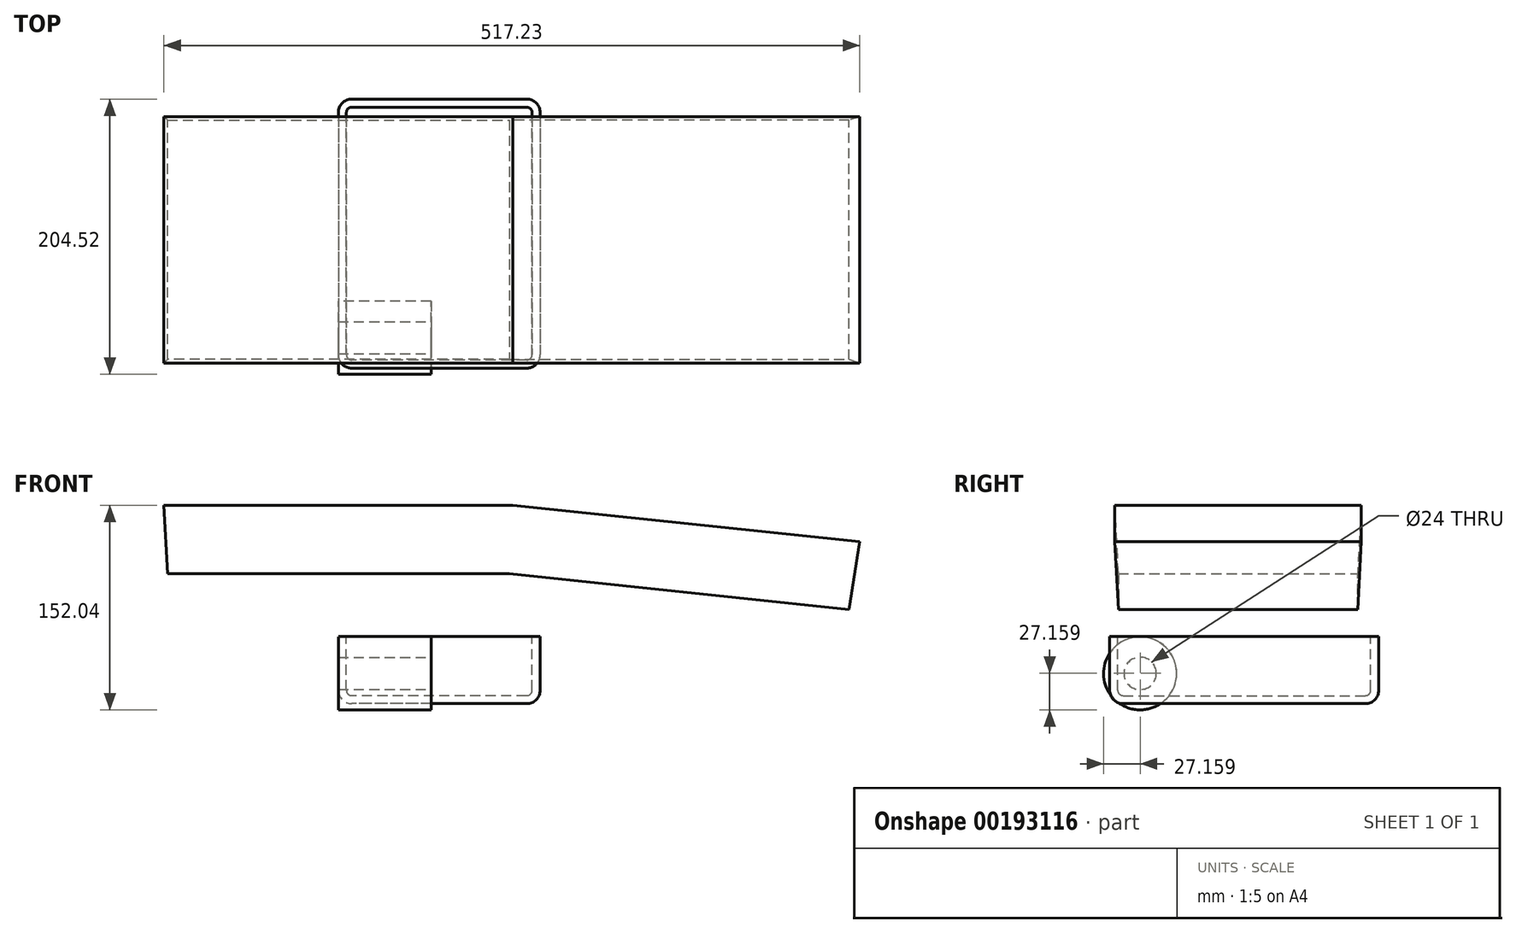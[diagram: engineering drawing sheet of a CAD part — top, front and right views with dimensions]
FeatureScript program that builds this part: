
annotation { "Feature Type Name" : "Feature", "Feature Type Description" : "" }
export const myFeature = defineFeature(function(context is Context, id is Id, definition is map)
    precondition{}
    {
        {
            var Q0;
            Q0=qCreatedBy(makeId("Top.planeOp"),FACE);
            var sketch = newSketch(context, id + "F0", { "sketchPlane" : qUnion([Q0])});
            skLineSegment(sketch, "E0.bottom", {"start": v(127, 88.9) * mm, "end": v(-127, 88.9) * mm});
            skLineSegment(sketch, "E0.top", {"start": v(127, -88.9) * mm, "end": v(-127, -88.9) * mm});
            skLineSegment(sketch, "E0.left", {"start": v(127, 88.9) * mm, "end": v(127, -88.9) * mm});
            skLineSegment(sketch, "E0.right", {"start": v(-127, 88.9) * mm, "end": v(-127, -88.9) * mm});
            skPoint(sketch, "E0.middle", {"position": v(0, 0) * mm});
            skSolve(sketch);
        }
        {
            var Q0;
            Q0=makeQuery(id+"F0.imprint","IMPRINT",FACE,{"disambiguationData":[TD([[makeQuery(id+"F0.imprint","IMPRINT",EDGE,{"derivedFrom":sQuery(id+"F0.wireOp",EDGE,"E0.bottom")}),1.0]])]});
            extrude(context, id + "F1", {"entities" : qUnion([Q0]), "depth" : 50.8 * mm, "hasDraft" : true, "draftAngle" : 3 * degree});
        }
        {
            var Q0;
            Q0=makeQuery(id+"F1.opExtrude","SWEPT_BODY",BODY,{"disambiguationData":[OSD([sQuery(id+"F0.wireOp",EDGE,"E0.bottom"),sQuery(id+"F0.wireOp",EDGE,"E0.top"),sQuery(id+"F0.wireOp",EDGE,"E0.left"),sQuery(id+"F0.wireOp",EDGE,"E0.right")])]});
            var Q1;
            Q1=makeQuery(id+"F1.opExtrude","SWEPT_FACE",FACE,{"disambiguationData":[OSD([sQuery(id+"F0.wireOp",EDGE,"E0.left")])]});
            mirror(context, id + "F2", {"operationType" : NewBodyOperationType.ADD, "entities" : qUnion([Q0]), "mirrorPlane" : qUnion([Q1])});
        }
        {
            var Q0;
            Q0=qCreatedBy(makeId("Right.planeOp"),FACE);
            var sketch = newSketch(context, id + "F3", { "sketchPlane" : qUnion([Q0])});
            skCircle(sketch, "E1", {"center": v(-72.75, -74.08) * mm, "radius": 27.15 * mm});
            skSolve(sketch);
        }
        {
            var Q0;
            Q0=makeQuery(id+"F3.imprint","IMPRINT",FACE,{"disambiguationData":[TD([[makeQuery(id+"F3.imprint","IMPRINT",EDGE,{"derivedFrom":sQuery(id+"F3.wireOp",EDGE,"E1")}),1.0]])]});
            extrude(context, id + "F4", {"entities" : qUnion([Q0]), "depth" : 69 * mm});
        }
        {
            var Q0;
            Q0=makeQuery(id+"F4.opExtrude","CAP_FACE",FACE,{"disambiguationData":[OSD([sQuery(id+"F3.wireOp",EDGE,"E1")])],"isStart":false});
            var sketch = newSketch(context, id + "F5", { "sketchPlane" : qUnion([Q0])});
            skCircle(sketch, "E2", {"center": v(-72.75, -74.08) * mm, "radius": 12 * mm});
            skSolve(sketch);
        }
        {
            var Q0;
            Q0 = qSketchRegion(id + "F5", true);
            extrude(context, id + "F6", {"entities" : qUnion([Q0]), "operationType" : NewBodyOperationType.REMOVE, "endBound" : BoundingType.THROUGH_ALL, "oppositeDirection" : true, "depth" : 25 * mm});
        }
        {
            var Q0;
            Q0=makeQuery(id+"F2.opPattern","COPY",FACE,{"derivedFrom":makeQuery(id+"F1.opExtrude","CAP_FACE",FACE,{"disambiguationData":[OSD([sQuery(id+"F0.wireOp",EDGE,"E0.bottom"),sQuery(id+"F0.wireOp",EDGE,"E0.top"),sQuery(id+"F0.wireOp",EDGE,"E0.left"),sQuery(id+"F0.wireOp",EDGE,"E0.right")])],"isStart":false}),"instanceName":"1"});
            var sketch = newSketch(context, id + "F11", { "sketchPlane" : qUnion([Q0])});
            skLineSegment(sketch, "E3.bottom", {"start": v(222.83, 45.58) * mm, "end": v(281.51, 45.58) * mm});
            skLineSegment(sketch, "E3.top", {"start": v(222.83, 91.56) * mm, "end": v(281.51, 91.56) * mm});
            skLineSegment(sketch, "E3.left", {"start": v(222.83, 45.58) * mm, "end": v(222.83, 91.56) * mm});
            skLineSegment(sketch, "E3.right", {"start": v(281.51, 45.58) * mm, "end": v(281.51, 91.56) * mm});
            skSolve(sketch);
        }
        {
            var Q0;
            Q0=sQuery(id+"F11.wireOp",EDGE,"E3.bottom");
            var Q1;
            Q1=sQuery(id+"F11.wireOp",EDGE,"E3.left");
            var Q2;
            Q2=sQuery(id+"F11.wireOp",EDGE,"E3.right");
            var Q3;
            Q3=sQuery(id+"F11.wireOp",EDGE,"E3.top");
            extrude(context, id + "F7", {"bodyType" : ToolBodyType.SURFACE, "surfaceEntities" : qUnion([Q0, Q1, Q2, Q3]), "depth" : 100 * mm});
        }
        {
            var Q0;
            Q0=makeQuery(id+"F7.opExtrude","SWEPT_BODY",BODY,{"disambiguationData":[OSD([sQuery(id+"F11.wireOp",EDGE,"E3.left")])]});
            deleteBodies(context, id + "F12", {"entities" : qUnion([Q0])});
        }
        {
            var Q0;
            Q0=qCreatedBy(makeId("Right.planeOp"),FACE);
            var sketch = newSketch(context, id + "F13", { "sketchPlane" : qUnion([Q0])});
            skLineSegment(sketch, "E4.bottom", {"start": v(104.61, -46.62) * mm, "end": v(-95.39, -46.62) * mm});
            skLineSegment(sketch, "E4.top", {"start": v(104.61, -96.62) * mm, "end": v(-95.39, -96.62) * mm});
            skLineSegment(sketch, "E4.left", {"start": v(104.61, -46.62) * mm, "end": v(104.61, -96.62) * mm});
            skLineSegment(sketch, "E4.right", {"start": v(-95.39, -46.62) * mm, "end": v(-95.39, -96.62) * mm});
            skSolve(sketch);
        }
        {
            var Q0;
            Q0=makeQuery(id+"F13.imprint","IMPRINT",FACE,{"disambiguationData":[TD([[makeQuery(id+"F13.imprint","IMPRINT",EDGE,{"derivedFrom":sQuery(id+"F13.wireOp",EDGE,"E4.bottom")}),1.0]])]});
            extrude(context, id + "F8", {"entities" : qUnion([Q0]), "depth" : 150 * mm});
        }
        {
            var Q0;
            Q0=makeQuery(id+"F8.opExtrude","CAP_EDGE",EDGE,{"disambiguationData":[OSD([sQuery(id+"F13.wireOp",EDGE,"E4.right")])],"isStart":true});
            var Q1;
            Q1=makeQuery(id+"F8.opExtrude","CAP_EDGE",EDGE,{"disambiguationData":[OSD([sQuery(id+"F13.wireOp",EDGE,"E4.right")])],"isStart":false});
            var Q2;
            Q2=makeQuery(id+"F8.opExtrude","CAP_EDGE",EDGE,{"disambiguationData":[OSD([sQuery(id+"F13.wireOp",EDGE,"E4.left")])],"isStart":true});
            var Q3;
            Q3=makeQuery(id+"F8.opExtrude","CAP_EDGE",EDGE,{"disambiguationData":[OSD([sQuery(id+"F13.wireOp",EDGE,"E4.left")])],"isStart":false});
            var Q4;
            Q4=makeQuery(id+"F8.opExtrude","SWEPT_FACE",FACE,{"disambiguationData":[OSD([sQuery(id+"F13.wireOp",EDGE,"E4.top")])]});
            fillet(context, id + "F9", {"entities" : qUnion([Q0, Q1, Q2, Q3, Q4]), "radius" : 10 * mm, "tangentPropagation" : true, "allowEdgeOverflow" : false});
        }
        {
            var Q0;
            Q0=makeQuery(id+"F8.opExtrude","SWEPT_FACE",FACE,{"disambiguationData":[OSD([sQuery(id+"F13.wireOp",EDGE,"E4.bottom")])]});
            shell(context, id + "F10", {"entities" : qUnion([Q0]), "thickness" : 6 * mm});
        }
    });
